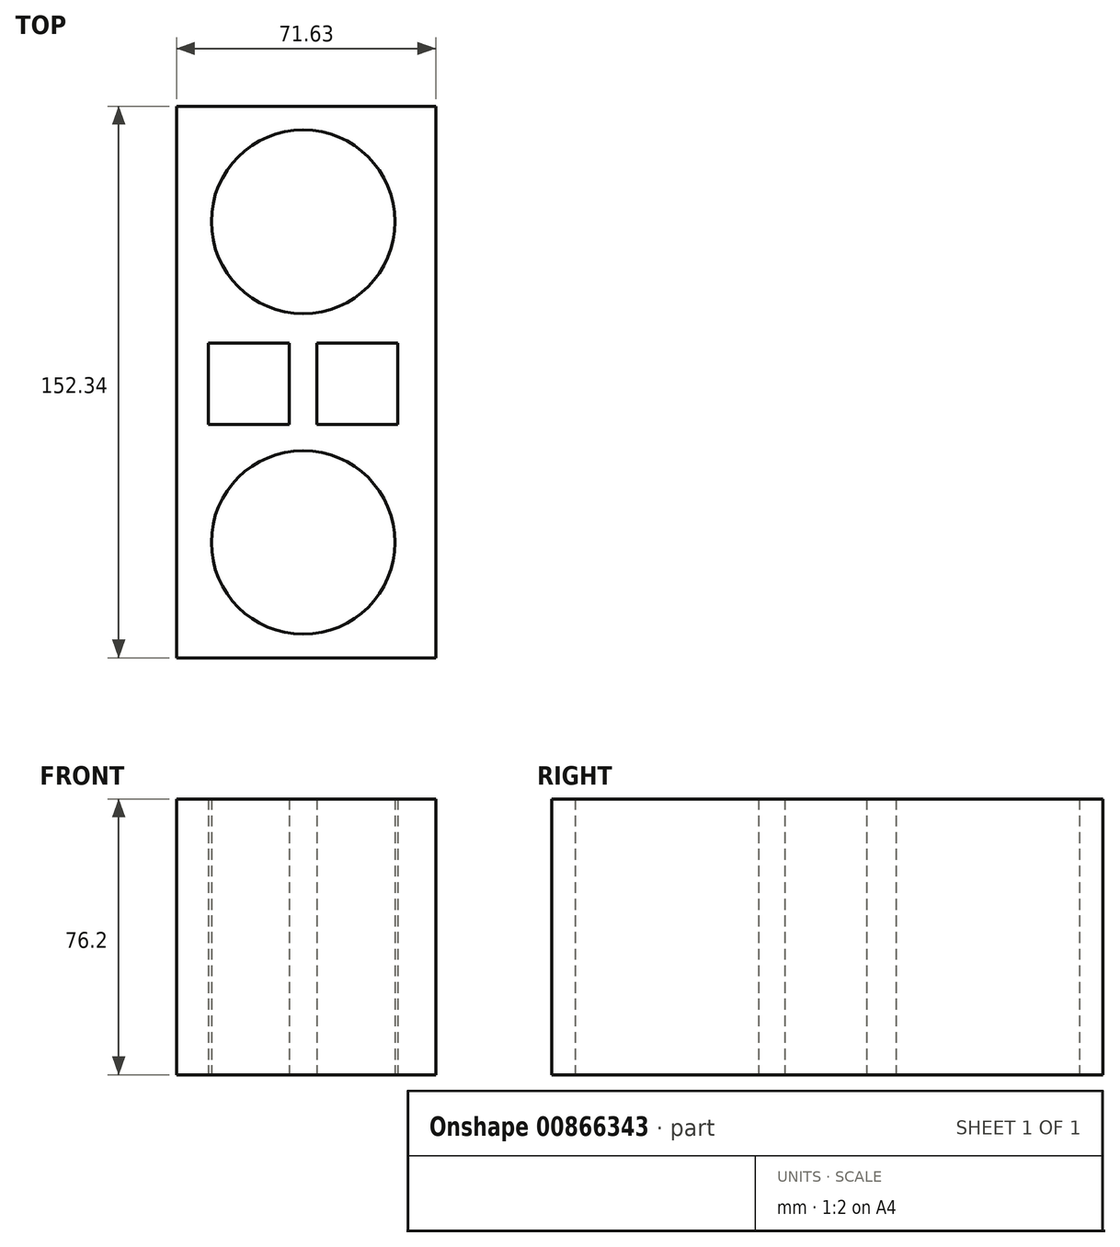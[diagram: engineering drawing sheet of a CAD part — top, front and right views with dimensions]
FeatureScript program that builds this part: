
annotation { "Feature Type Name" : "Feature", "Feature Type Description" : "" }
export const myFeature = defineFeature(function(context is Context, id is Id, definition is map)
    precondition{}
    {
        {
            var Q0;
            Q0=qCreatedBy(makeId("Top.planeOp"),FACE);
            var sketch = newSketch(context, id + "F0", { "sketchPlane" : qUnion([Q0])});
            skLineSegment(sketch, "E0.bottom", {"start": v(-35, 76.17) * mm, "end": v(36.63, 76.17) * mm});
            skLineSegment(sketch, "E0.top", {"start": v(-35, -76.17) * mm, "end": v(36.63, -76.17) * mm});
            skLineSegment(sketch, "E0.left", {"start": v(-35, 76.17) * mm, "end": v(-35, -76.17) * mm});
            skLineSegment(sketch, "E0.right", {"start": v(36.63, 76.17) * mm, "end": v(36.63, -76.17) * mm});
            skCircle(sketch, "E1", {"center": v(0, 44.3) * mm, "radius": 25.37 * mm});
            skCircle(sketch, "E2.MirrorC", {"center": v(0, -44.3) * mm, "radius": 25.37 * mm});
            skLineSegment(sketch, "E3.bottom", {"start": v(-26.17, 10.82) * mm, "end": v(-3.84, 10.82) * mm});
            skLineSegment(sketch, "E3.top", {"start": v(-26.17, -11.75) * mm, "end": v(-3.84, -11.75) * mm});
            skLineSegment(sketch, "E3.left", {"start": v(-26.17, 10.82) * mm, "end": v(-26.17, -11.75) * mm});
            skLineSegment(sketch, "E3.right", {"start": v(-3.84, 10.82) * mm, "end": v(-3.84, -11.75) * mm});
            skLineSegment(sketch, "E4.MirrorCS", {"start": v(3.84, 10.82) * mm, "end": v(3.84, -11.75) * mm});
            skLineSegment(sketch, "E5.MirrorCS", {"start": v(26.17, -11.75) * mm, "end": v(3.84, -11.75) * mm});
            skLineSegment(sketch, "E6.MirrorCS", {"start": v(26.17, 10.82) * mm, "end": v(26.17, -11.75) * mm});
            skLineSegment(sketch, "E7.MirrorCS", {"start": v(26.17, 10.82) * mm, "end": v(3.84, 10.82) * mm});
            skSolve(sketch);
        }
        {
            var Q0;
            Q0=qSketchRegion(id+"F0",true);
            extrude(context, id + "F1", {"entities" : qUnion([Q0]), "depth" : 76.2 * mm, "offsetDistance" : 25.4 * mm});
        }
    });
